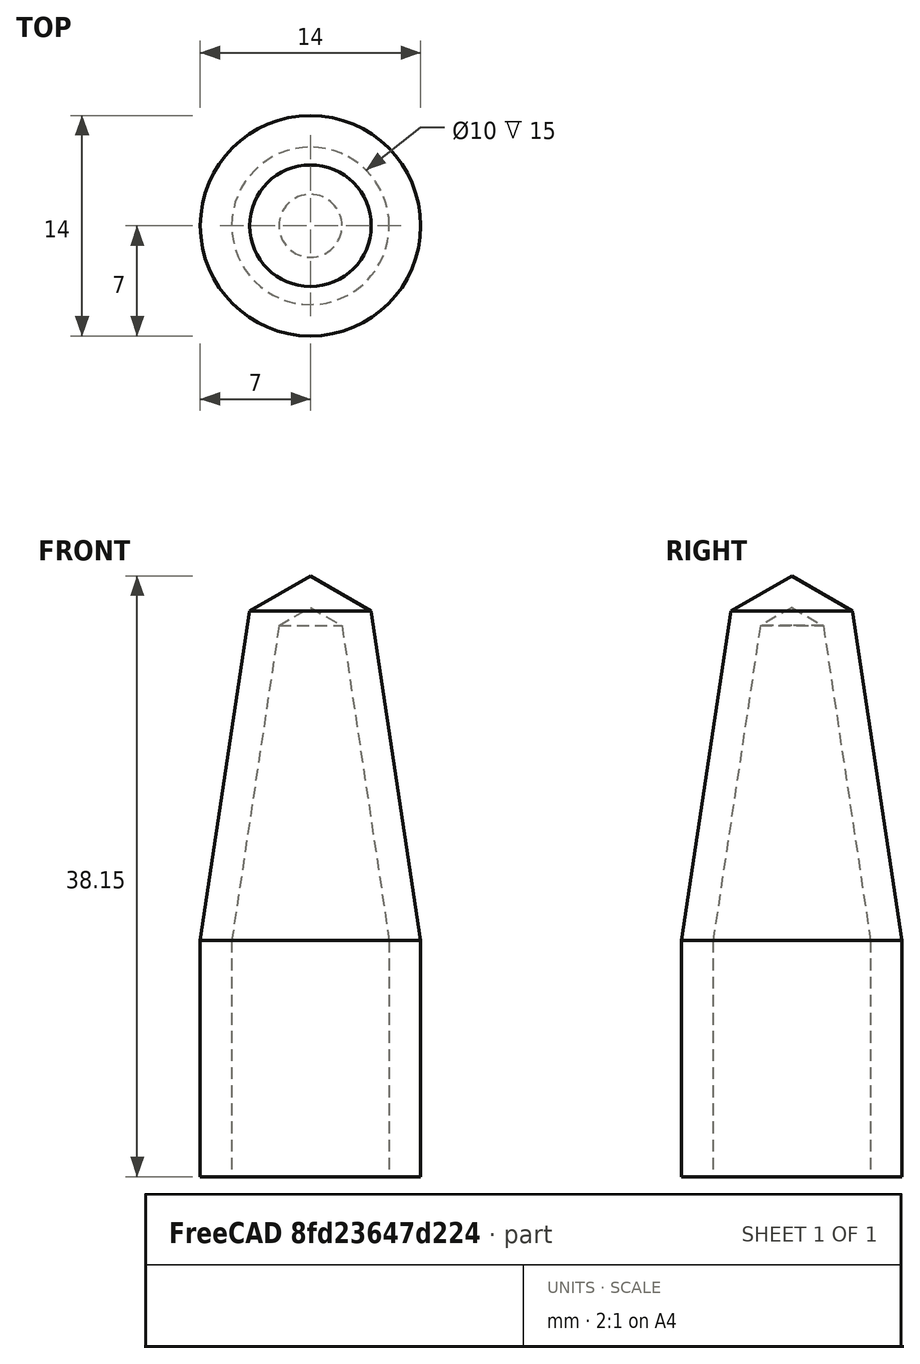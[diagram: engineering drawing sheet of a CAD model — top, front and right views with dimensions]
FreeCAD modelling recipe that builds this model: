
FCSTD DOCUMENT  (FreeCAD 0.20R29177 (Git))
Label: tubeDespensorCover
License: All rights reserved
LicenseURL: http://en.wikipedia.org/wiki/All_rights_reserved
objects: Sketcher::SketchObject×1, Spreadsheet::Sheet×1, PartDesign::Revolution×1, PartDesign::Body×1
note: 4 computed .brp shape members not serialized (recipe doc carries the construction recipe); baked Part::Feature solids carry a one-line shape summary decoded from their .brp

FEATURE [Sketcher::SketchObject] Sketch
  FullyConstrained = true
  MapMode = 5
  Placement = pos=(0,0,0) rot=(1,0,0;1.5708rad)
  Support = -> [XZ_Plane]
  expr: Constraints[12] = Spreadsheet.midR
  expr: Constraints[19] = Spreadsheet.wallThickness
  expr: Constraints[21] = Spreadsheet.topR
  expr: Constraints[22] = Spreadsheet.topHeight
  expr: Constraints[6] = Spreadsheet.wallThickness
  expr: Constraints[8] = Spreadsheet.bottomInnerR
  expr: Constraints[9] = Spreadsheet.bottomHeight
  sketch-geometry (8):
    g0: LineSegment StartX=-3.86118 StartY=35.9254 StartZ=0 EndX=-7 EndY=15 EndZ=0
    g1: LineSegment StartX=-7 StartY=15 StartZ=0 EndX=-7 EndY=0 EndZ=0
    g2: LineSegment StartX=-2 StartY=35 StartZ=0 EndX=-5 EndY=15 EndZ=0
    g3: LineSegment StartX=-5 StartY=15 StartZ=0 EndX=-5 EndY=0 EndZ=0
    g4: LineSegment StartX=-7 StartY=0 StartZ=0 EndX=-5 EndY=0 EndZ=0
    g5: LineSegment StartX=-3.86118 StartY=35.9254 StartZ=0 EndX=0 EndY=38.1547 EndZ=0
    g6: LineSegment StartX=-2 StartY=35 StartZ=0 EndX=0 EndY=36.1547 EndZ=0
    g7: LineSegment StartX=0 StartY=38.1547 StartZ=0 EndX=0 EndY=36.1547 EndZ=0
  constraints (24):
    c: Coincident(g1,g0)
    c: PointOnObject(g1,g-1)
    c: Coincident(g3,g2)
    c: PointOnObject(g3,g-1)
    c: Coincident(g4,g1)
    c: Coincident(g4,g3)
    c: DistanceX(g4,g4) = 2
    c: Parallel(g0,g2)
    c: DistanceX(g3,g-1) = 5
    c: DistanceY(g3,g3) = 15
    c: Parallel(g3,g1)
    c: Equal(g3,g1)
    c: DistanceX(g2,g-1) = 5
    c: Coincident(g5,g0)
    c: PointOnObject(g5,g-2)
    c: Coincident(g6,g2)
    c: Coincident(g7,g5)
    c: Coincident(g7,g6)
    c: PointOnObject(g6,g-2)
    c: DistanceY(g7,g7) = 2
    c: Parallel(g6,g5)
    c: DistanceX(g2,g-1) = 2
    c: DistanceY(g2,g2) = 20
    c: Angle(g-1,g6) = 0.523599
FEATURE [Spreadsheet::Sheet] Spreadsheet
  cells = A2=wallThickness; B2(wallThickness)=2; A3=bottomInnerR; B3(bottomInnerR)=5; A4=height; B4(height)=25; A5=baseAngle; B5(baseAngle)=85; A6=topR; B6(topR)=2; A7=midR; B7(midR)=5; A8=topHeight; B8(topHeight)=20; A9=bottomHeight; B9(bottomHeight)=15
FEATURE [PartDesign::Revolution] Revolution
  Angle = 360
  Axis = (0,2e-16,1)
  Base = (0,0,0)
  Placement = pos=(0,0,0) rot=(1,0,0;1.5708rad)
  Profile = -> Sketch
  ReferenceAxis = -> Sketch [V_Axis]
FEATURE [PartDesign::Body] Body
  Group = -> [Sketch,Revolution]
  Origin = -> Origin
  Tip = -> Revolution
